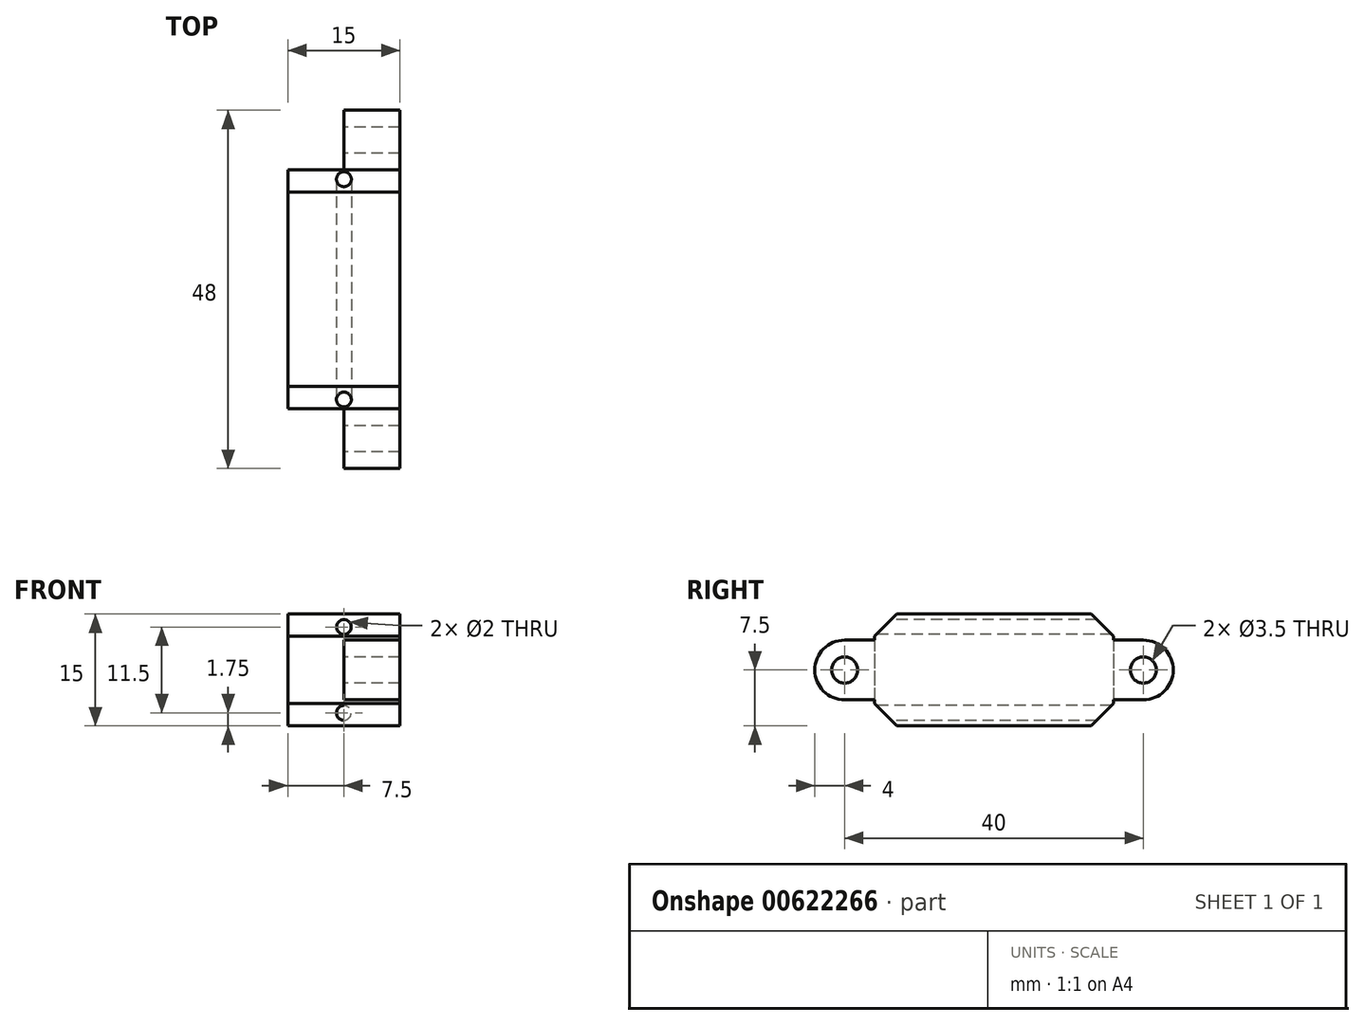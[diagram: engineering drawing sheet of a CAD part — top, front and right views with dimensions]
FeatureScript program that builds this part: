
annotation { "Feature Type Name" : "Feature", "Feature Type Description" : "" }
export const myFeature = defineFeature(function(context is Context, id is Id, definition is map)
    precondition{}
    {
        {
            var Q0;
            Q0=qCreatedBy(makeId("Right.planeOp"),FACE);
            var sketch = newSketch(context, id + "F0", { "sketchPlane" : qUnion([Q0])});
            skLineSegment(sketch, "E0.bottom", {"start": v(20, 4) * mm, "end": v(-20, 4) * mm});
            skLineSegment(sketch, "E0.top", {"start": v(20, -4) * mm, "end": v(-20, -4) * mm});
            skLineSegment(sketch, "E0.left", {"start": v(20, 4) * mm, "end": v(20, -4) * mm});
            skLineSegment(sketch, "E0.right", {"start": v(-20, 4) * mm, "end": v(-20, -4) * mm});
            skPoint(sketch, "E0.middle", {"position": v(0, 0) * mm});
            skCircle(sketch, "E1", {"center": v(-20, 0) * mm, "radius": 4 * mm});
            skCircle(sketch, "E2", {"center": v(20, 0) * mm, "radius": 4 * mm});
            skLineSegment(sketch, "E3.bottom", {"start": v(16, 7.5) * mm, "end": v(-16, 7.5) * mm});
            skLineSegment(sketch, "E3.top", {"start": v(16, -7.5) * mm, "end": v(-16, -7.5) * mm});
            skLineSegment(sketch, "E3.left", {"start": v(16, 7.5) * mm, "end": v(16, -7.5) * mm});
            skLineSegment(sketch, "E3.right", {"start": v(-16, 7.5) * mm, "end": v(-16, -7.5) * mm});
            skCircle(sketch, "E4", {"center": v(-20, 0) * mm, "radius": 1.75 * mm});
            skCircle(sketch, "E5", {"center": v(20, 0) * mm, "radius": 1.75 * mm});
            skSolve(sketch);
        }
        {
            var Q0;
            {var subQ5=sQuery(id+"F0.wireOp",EDGE,"E3.top");Q0=makeQuery(id+"F0.imprint","IMPRINT",FACE,{"disambiguationData":[TD([[makeQuery(id+"F0.imprint","IMPRINT",EDGE,{"derivedFrom":subQ5}),-1.0]])]});}
            var Q1;
            {var subQ0=sQuery(id+"F0.wireOp",EDGE,"E3.left");var subQ7=sQuery(id+"F0.wireOp",EDGE,"E0.bottom");var subQ8=makeQuery(id+"F0.imprint","INTERSECT",VERTEX,{"derivedFrom":[subQ7,subQ0]});Q1=makeQuery(id+"F0.imprint","IMPRINT",FACE,{"disambiguationData":[TD([[makeQuery(id+"F0.imprint","IMPRINT",EDGE,{"disambiguationData":[TD([[subQ8,-1.0]])],"derivedFrom":subQ7}),1.0]])]});}
            var Q2;
            {var subQ5=sQuery(id+"F0.wireOp",EDGE,"E3.bottom");Q2=makeQuery(id+"F0.imprint","IMPRINT",FACE,{"disambiguationData":[TD([[makeQuery(id+"F0.imprint","IMPRINT",EDGE,{"derivedFrom":subQ5}),1.0]])]});}
            extrude(context, id + "F1", {"entities" : qUnion([Q0, Q1, Q2]), "endBound" : BoundingType.SYMMETRIC, "depth" : 15 * mm, "offsetDistance" : 25 * mm});
        }
        {
            var Q0;
            {var subQ1=sQuery(id+"F0.wireOp",EDGE,"E0.top");var subQ3=sQuery(id+"F0.wireOp",EDGE,"E3.right");var subQ4=makeQuery(id+"F0.imprint","INTERSECT",VERTEX,{"derivedFrom":[subQ1,subQ3]});Q0=makeQuery(id+"F0.imprint","IMPRINT",FACE,{"disambiguationData":[TD([[makeQuery(id+"F0.imprint","IMPRINT",EDGE,{"disambiguationData":[TD([[subQ4,1.0]])],"derivedFrom":subQ3}),-1.0]])]});}
            var Q1;
            {var subQ1=sQuery(id+"F0.wireOp",EDGE,"E0.right");var subQ5=sQuery(id+"F0.wireOp",EDGE,"E4");var subQ7=makeQuery(id+"F0.imprint","INTERSECT",VERTEX,{"disambiguationData":[OD(0.0)],"derivedFrom":[subQ1,subQ5]});Q1=makeQuery(id+"F0.imprint","IMPRINT",FACE,{"disambiguationData":[TD([[makeQuery(id+"F0.imprint","IMPRINT",EDGE,{"disambiguationData":[TD([[subQ7,1.0]])],"derivedFrom":subQ5}),-1.0]])]});}
            var Q2;
            {var subQ1=sQuery(id+"F0.wireOp",EDGE,"E0.bottom");var subQ3=sQuery(id+"F0.wireOp",EDGE,"E3.right");var subQ4=makeQuery(id+"F0.imprint","INTERSECT",VERTEX,{"derivedFrom":[subQ1,subQ3]});Q2=makeQuery(id+"F0.imprint","IMPRINT",FACE,{"disambiguationData":[TD([[makeQuery(id+"F0.imprint","IMPRINT",EDGE,{"disambiguationData":[TD([[subQ4,-1.0]])],"derivedFrom":subQ3}),-1.0]])]});}
            var Q3;
            {var subQ1=sQuery(id+"F0.wireOp",EDGE,"E0.right");var subQ3=sQuery(id+"F0.wireOp",EDGE,"E4");var subQ4=makeQuery(id+"F0.imprint","INTERSECT",VERTEX,{"disambiguationData":[OD(0.0)],"derivedFrom":[subQ1,subQ3]});Q3=makeQuery(id+"F0.imprint","IMPRINT",FACE,{"disambiguationData":[TD([[makeQuery(id+"F0.imprint","IMPRINT",EDGE,{"disambiguationData":[TD([[subQ4,-1.0]])],"derivedFrom":subQ3}),-1.0]])]});}
            var Q4;
            {var subQ1=sQuery(id+"F0.wireOp",EDGE,"E0.left");var subQ5=sQuery(id+"F0.wireOp",EDGE,"E5");var subQ7=makeQuery(id+"F0.imprint","INTERSECT",VERTEX,{"disambiguationData":[OD(0.0)],"derivedFrom":[subQ1,subQ5]});Q4=makeQuery(id+"F0.imprint","IMPRINT",FACE,{"disambiguationData":[TD([[makeQuery(id+"F0.imprint","IMPRINT",EDGE,{"disambiguationData":[TD([[subQ7,-1.0]])],"derivedFrom":subQ5}),-1.0]])]});}
            var Q5;
            {var subQ1=sQuery(id+"F0.wireOp",EDGE,"E0.bottom");var subQ3=sQuery(id+"F0.wireOp",EDGE,"E3.left");var subQ4=makeQuery(id+"F0.imprint","INTERSECT",VERTEX,{"derivedFrom":[subQ1,subQ3]});Q5=makeQuery(id+"F0.imprint","IMPRINT",FACE,{"disambiguationData":[TD([[makeQuery(id+"F0.imprint","IMPRINT",EDGE,{"disambiguationData":[TD([[subQ4,-1.0]])],"derivedFrom":subQ3}),1.0]])]});}
            var Q6;
            {var subQ1=sQuery(id+"F0.wireOp",EDGE,"E0.top");var subQ3=sQuery(id+"F0.wireOp",EDGE,"E3.left");var subQ4=makeQuery(id+"F0.imprint","INTERSECT",VERTEX,{"derivedFrom":[subQ1,subQ3]});Q6=makeQuery(id+"F0.imprint","IMPRINT",FACE,{"disambiguationData":[TD([[makeQuery(id+"F0.imprint","IMPRINT",EDGE,{"disambiguationData":[TD([[subQ4,1.0]])],"derivedFrom":subQ3}),1.0]])]});}
            var Q7;
            {var subQ1=sQuery(id+"F0.wireOp",EDGE,"E0.left");var subQ3=sQuery(id+"F0.wireOp",EDGE,"E5");var subQ4=makeQuery(id+"F0.imprint","INTERSECT",VERTEX,{"disambiguationData":[OD(0.0)],"derivedFrom":[subQ1,subQ3]});Q7=makeQuery(id+"F0.imprint","IMPRINT",FACE,{"disambiguationData":[TD([[makeQuery(id+"F0.imprint","IMPRINT",EDGE,{"disambiguationData":[TD([[subQ4,1.0]])],"derivedFrom":subQ3}),-1.0]])]});}
            extrude(context, id + "F2", {"entities" : qUnion([Q0, Q1, Q2, Q3, Q4, Q5, Q6, Q7]), "operationType" : NewBodyOperationType.ADD, "depth" : 7.5 * mm, "offsetDistance" : 25 * mm});
        }
        {
            var Q0;
            Q0=makeQuery(id+"F1.opExtrude","SWEPT_FACE",FACE,{"disambiguationData":[OSD([sQuery(id+"F0.wireOp",EDGE,"E3.right")])]});
            var sketch = newSketch(context, id + "F3", { "sketchPlane" : qUnion([Q0])});
            skLineSegment(sketch, "E6", {"start": v(0, 7.5) * mm, "end": v(0, 4) * mm});
            skCircle(sketch, "E7", {"center": v(0, 5.75) * mm, "radius": 1 * mm});
            skLineSegment(sketch, "E8", {"start": v(0, -4) * mm, "end": v(0, -7.5) * mm});
            skCircle(sketch, "E9", {"center": v(0, -5.75) * mm, "radius": 1 * mm});
            skSolve(sketch);
        }
        {
            var Q0;
            Q0 = qSketchRegion(id + "F3", true);
            extrude(context, id + "F4", {"entities" : qUnion([Q0]), "operationType" : NewBodyOperationType.REMOVE, "oppositeDirection" : true, "depth" : 40 * mm, "offsetDistance" : 25 * mm});
        }
        {
            var Q0;
            Q0=makeQuery(id+"F1.opExtrude","SWEPT_EDGE",EDGE,{"disambiguationData":[OSD([sQuery(id+"F0.wireOp",EDGE,"E3.bottom"),sQuery(id+"F0.wireOp",EDGE,"E3.right")])]});
            var Q1;
            Q1=makeQuery(id+"F1.opExtrude","SWEPT_EDGE",EDGE,{"disambiguationData":[OSD([sQuery(id+"F0.wireOp",EDGE,"E3.top"),sQuery(id+"F0.wireOp",EDGE,"E3.right")])]});
            var Q2;
            Q2=makeQuery(id+"F1.opExtrude","SWEPT_EDGE",EDGE,{"disambiguationData":[OSD([sQuery(id+"F0.wireOp",EDGE,"E3.bottom"),sQuery(id+"F0.wireOp",EDGE,"E3.left")])]});
            var Q3;
            Q3=makeQuery(id+"F1.opExtrude","SWEPT_EDGE",EDGE,{"disambiguationData":[OSD([sQuery(id+"F0.wireOp",EDGE,"E3.top"),sQuery(id+"F0.wireOp",EDGE,"E3.left")])]});
            chamfer(context, id + "F5", {"entities" : qUnion([Q0, Q1, Q2, Q3]), "width" : 3 * mm, "tangentPropagation" : true});
        }
    });
